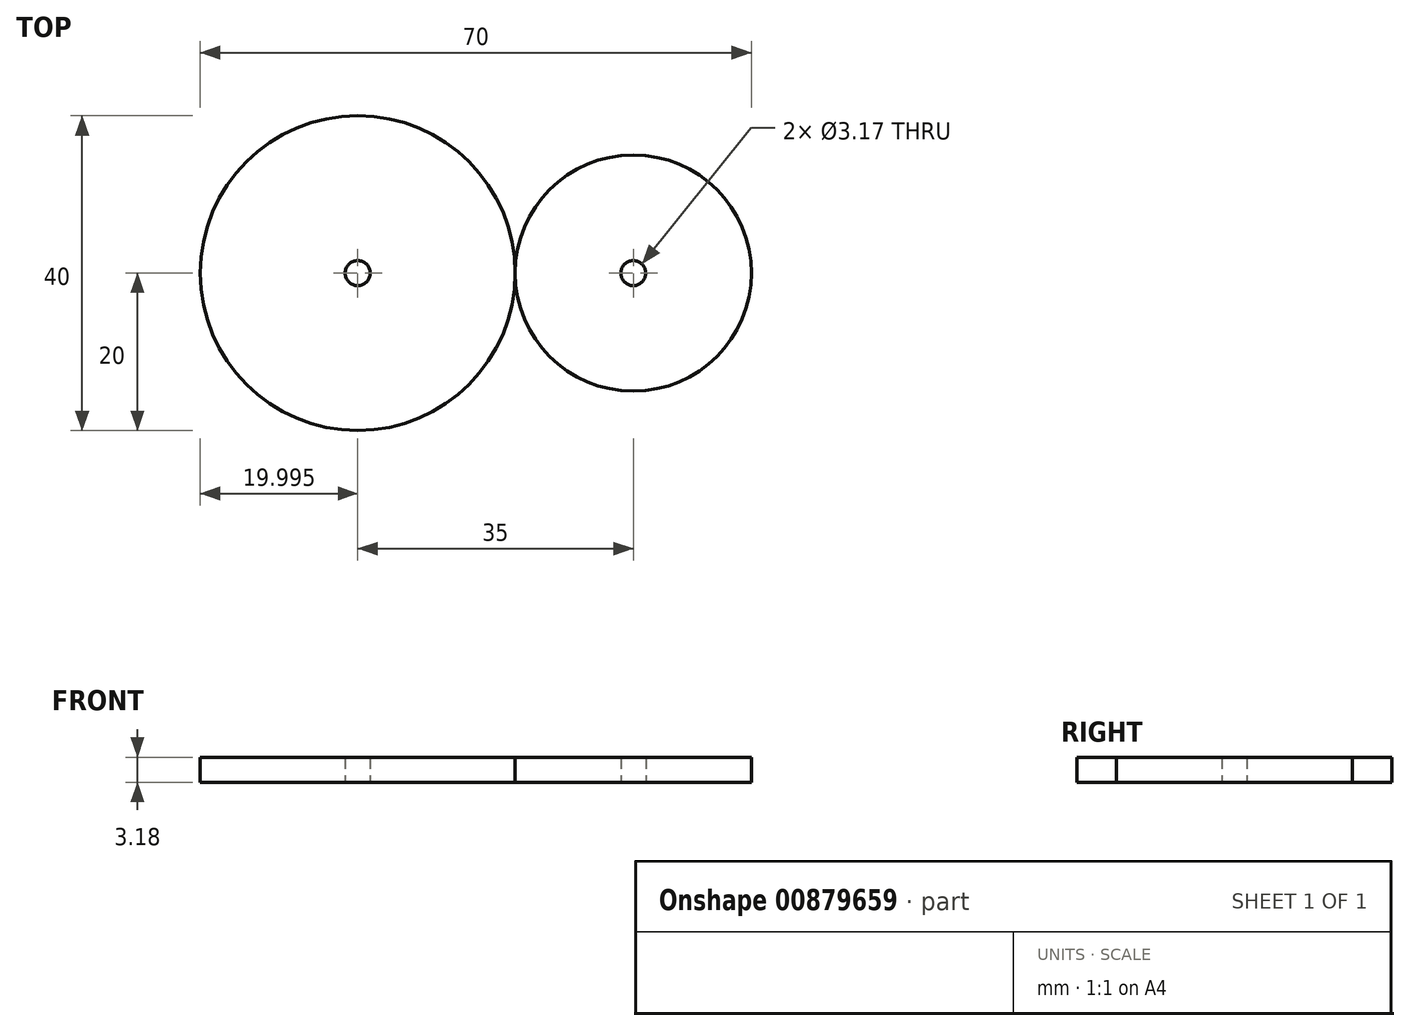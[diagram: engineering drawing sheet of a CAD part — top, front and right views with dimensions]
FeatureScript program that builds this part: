
annotation { "Feature Type Name" : "Feature", "Feature Type Description" : "" }
export const myFeature = defineFeature(function(context is Context, id is Id, definition is map)
    precondition{}
    {
        {
            var Q0;
            Q0=qCreatedBy(makeId("Top.planeOp"),FACE);
            var sketch = newSketch(context, id + "F0", { "sketchPlane" : qUnion([Q0])});
            skCircle(sketch, "E0", {"center": v(-43.17, 10.61) * mm, "radius": 20 * mm});
            skCircle(sketch, "E1", {"center": v(-8.17, 10.61) * mm, "radius": 15 * mm});
            skSolve(sketch);
        }
        {
            var Q0;
            Q0=makeQuery(id+"F0.imprint","IMPRINT",FACE,{"disambiguationData":[TD([[makeQuery(id+"F0.imprint","IMPRINT",EDGE,{"derivedFrom":sQuery(id+"F0.wireOp",EDGE,"E0")}),1.0]])]});
            var Q1;
            Q1=makeQuery(id+"F0.imprint","IMPRINT",FACE,{"disambiguationData":[TD([[makeQuery(id+"F0.imprint","IMPRINT",EDGE,{"derivedFrom":sQuery(id+"F0.wireOp",EDGE,"E1")}),1.0]])]});
            extrude(context, id + "F1", {"entities" : qUnion([Q0, Q1]), "depth" : 3.17 * mm, "offsetDistance" : 25.4 * mm});
        }
        {
            var Q0;
            Q0=sQuery(id+"F0.wireOp",VERTEX,"E0.center");
            var Q1;
            Q1=sQuery(id+"F0.wireOp",VERTEX,"E1.center");
            var Q2;
            Q2=makeQuery(id+"F1.opExtrude","SWEPT_BODY",BODY,{"disambiguationData":[OSD([sQuery(id+"F0.wireOp",EDGE,"E0")])]});
            var Q3;
            Q3=makeQuery(id+"F1.opExtrude","SWEPT_BODY",BODY,{"disambiguationData":[OSD([sQuery(id+"F0.wireOp",EDGE,"E1")])]});
            hole(context, id + "F2", {"style" : HoleStyle.SIMPLE, "endStyle" : HoleEndStyle.THROUGH, "oppositeDirection" : true, "holeDiameter" : 3.17 * mm, "majorDiameter" : 6.35 * mm, "isTappedThrough" : true, "tappedDepth" : 12.7 * mm, "tapClearance" : 3, "locations" : qUnion([Q0, Q1]), "scope" : qUnion([Q2, Q3])});
        }
    });
